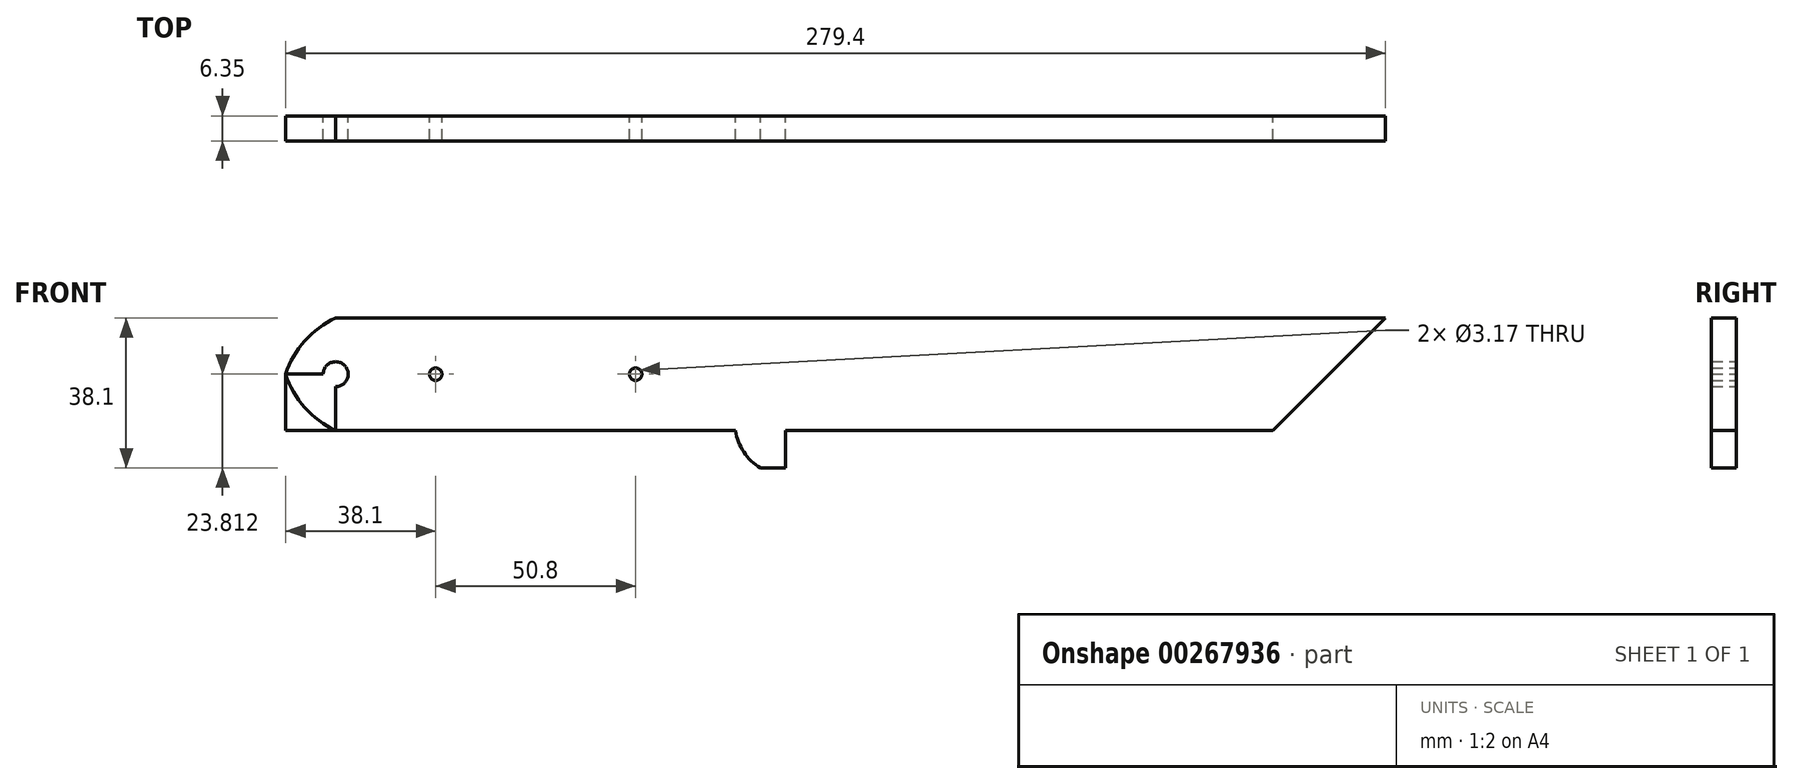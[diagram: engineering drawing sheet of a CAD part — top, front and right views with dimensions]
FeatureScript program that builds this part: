
annotation { "Feature Type Name" : "Feature", "Feature Type Description" : "" }
export const myFeature = defineFeature(function(context is Context, id is Id, definition is map)
    precondition{}
    {
        {
            var Q0;
            Q0=qCreatedBy(makeId("Front.planeOp"),FACE);
            var sketch = newSketch(context, id + "F0", { "sketchPlane" : qUnion([Q0])});
            skLineSegment(sketch, "E0.bottom", {"start": v(-139.7, 19.05) * mm, "end": v(139.7, 19.05) * mm});
            skLineSegment(sketch, "E0.top", {"start": v(-139.7, -19.05) * mm, "end": v(139.7, -19.05) * mm});
            skLineSegment(sketch, "E0.left", {"start": v(-139.7, 19.05) * mm, "end": v(-139.7, -19.05) * mm});
            skLineSegment(sketch, "E0.right", {"start": v(139.7, 19.05) * mm, "end": v(139.7, -19.05) * mm});
            skPoint(sketch, "E0.middle", {"position": v(0, 0) * mm});
            skLineSegment(sketch, "E1", {"start": v(-25.4, 19.05) * mm, "end": v(-25.4, -19.05) * mm});
            skLineSegment(sketch, "E2", {"start": v(-12.7, 19.05) * mm, "end": v(-12.7, -19.05) * mm});
            skLineSegment(sketch, "E3", {"start": v(-19.05, 19.05) * mm, "end": v(-19.05, -19.05) * mm});
            skArc(sketch, "E4", {"start": v(-25.4, -9.52) * mm, "mid": v(-23.32, -15.02) * mm, "end": v(-19.05, -19.05) * mm});
            skLineSegment(sketch, "E5", {"start": v(-25.4, -9.53) * mm, "end": v(-139.7, -9.52) * mm});
            skLineSegment(sketch, "E6", {"start": v(-127, 19.05) * mm, "end": v(-127, -19.05) * mm});
            skLineSegment(sketch, "E7", {"start": v(-139.7, 4.76) * mm, "end": v(-127, 4.76) * mm});
            skPoint(sketch, "E7.endSnap0", {"position": v(-127, 0) * mm});
            skArc(sketch, "E8", {"start": v(-127, 19.05) * mm, "mid": v(-134.86, 13.25) * mm, "end": v(-139.7, 4.76) * mm});
            skArc(sketch, "E9.MirrorCS", {"start": v(-127, -9.52) * mm, "mid": v(-134.86, -3.72) * mm, "end": v(-139.7, 4.76) * mm});
            skLineSegment(sketch, "E10", {"start": v(-12.7, -9.53) * mm, "end": v(139.7, -9.53) * mm});
            skLineSegment(sketch, "E11", {"start": v(139.7, 19.05) * mm, "end": v(111.13, -9.52) * mm});
            skLineSegment(sketch, "E12", {"start": v(119.5, 19.05) * mm, "end": v(105.2, 4.76) * mm});
            skLineSegment(sketch, "E13", {"start": v(-12.7, 4.76) * mm, "end": v(105.2, 4.76) * mm});
            skLineSegment(sketch, "E14", {"start": v(-127, 4.76) * mm, "end": v(-25.4, 4.76) * mm});
            skCircle(sketch, "E15", {"center": v(-127, 4.76) * mm, "radius": 3.18 * mm});
            skCircle(sketch, "E16", {"center": v(-101.6, 4.76) * mm, "radius": 1.59 * mm});
            skCircle(sketch, "E17", {"center": v(-50.8, 4.76) * mm, "radius": 1.59 * mm});
            skSolve(sketch);
        }
        {
            var Q0;
            {var subQ0=sQuery(id+"F0.wireOp",EDGE,"E15");var subQ1=sQuery(id+"F0.wireOp",EDGE,"E14");var subQ2=makeQuery(id+"F0.imprint","INTERSECT",VERTEX,{"derivedFrom":[subQ1,subQ0]});Q0=makeQuery(id+"F0.imprint","IMPRINT",FACE,{"disambiguationData":[TD([[makeQuery(id+"F0.imprint","IMPRINT",EDGE,{"disambiguationData":[TD([[subQ2,-1.0]])],"derivedFrom":subQ1}),-1.0]])]});}
            var Q1;
            {var subQ9=sQuery(id+"F0.wireOp",EDGE,"E0.bottom");var subQ12=sQuery(id+"F0.wireOp",EDGE,"E1");var subQ13=makeQuery(id+"F0.imprint","INTERSECT",VERTEX,{"derivedFrom":[subQ9,subQ12]});Q1=makeQuery(id+"F0.imprint","IMPRINT",FACE,{"disambiguationData":[TD([[makeQuery(id+"F0.imprint","IMPRINT",EDGE,{"disambiguationData":[TD([[subQ13,-1.0]])],"derivedFrom":subQ12}),-1.0]])]});}
            var Q2;
            {var subQ0=sQuery(id+"F0.wireOp",EDGE,"E8");Q2=makeQuery(id+"F0.imprint","IMPRINT",FACE,{"disambiguationData":[TD([[makeQuery(id+"F0.imprint","IMPRINT",EDGE,{"derivedFrom":subQ0}),1.0]])]});}
            var Q3;
            {var subQ0=sQuery(id+"F0.wireOp",EDGE,"E9.MirrorCS");Q3=makeQuery(id+"F0.imprint","IMPRINT",FACE,{"disambiguationData":[TD([[makeQuery(id+"F0.imprint","IMPRINT",EDGE,{"derivedFrom":subQ0}),-1.0]])]});}
            var Q4;
            {var subQ5=sQuery(id+"F0.wireOp",EDGE,"E3");Q4=makeQuery(id+"F0.imprint","IMPRINT",FACE,{"disambiguationData":[TD([[makeQuery(id+"F0.imprint","IMPRINT",EDGE,{"derivedFrom":subQ5}),1.0]])]});}
            var Q5;
            {var subQ4=sQuery(id+"F0.wireOp",EDGE,"E3");Q5=makeQuery(id+"F0.imprint","IMPRINT",FACE,{"disambiguationData":[TD([[makeQuery(id+"F0.imprint","IMPRINT",EDGE,{"derivedFrom":subQ4}),-1.0]])]});}
            var Q6;
            {var subQ0=sQuery(id+"F0.wireOp",EDGE,"E11");Q6=makeQuery(id+"F0.imprint","IMPRINT",FACE,{"disambiguationData":[TD([[makeQuery(id+"F0.imprint","IMPRINT",EDGE,{"derivedFrom":subQ0}),-1.0]])]});}
            var Q7;
            {var subQ3=sQuery(id+"F0.wireOp",EDGE,"E12");Q7=makeQuery(id+"F0.imprint","IMPRINT",FACE,{"disambiguationData":[TD([[makeQuery(id+"F0.imprint","IMPRINT",EDGE,{"derivedFrom":subQ3}),-1.0]])]});}
            extrude(context, id + "F1", {"entities" : qUnion([Q0, Q1, Q2, Q3, Q4, Q5, Q6, Q7]), "depth" : 6.35 * mm, "offsetDistance" : 25.4 * mm});
        }
    });
